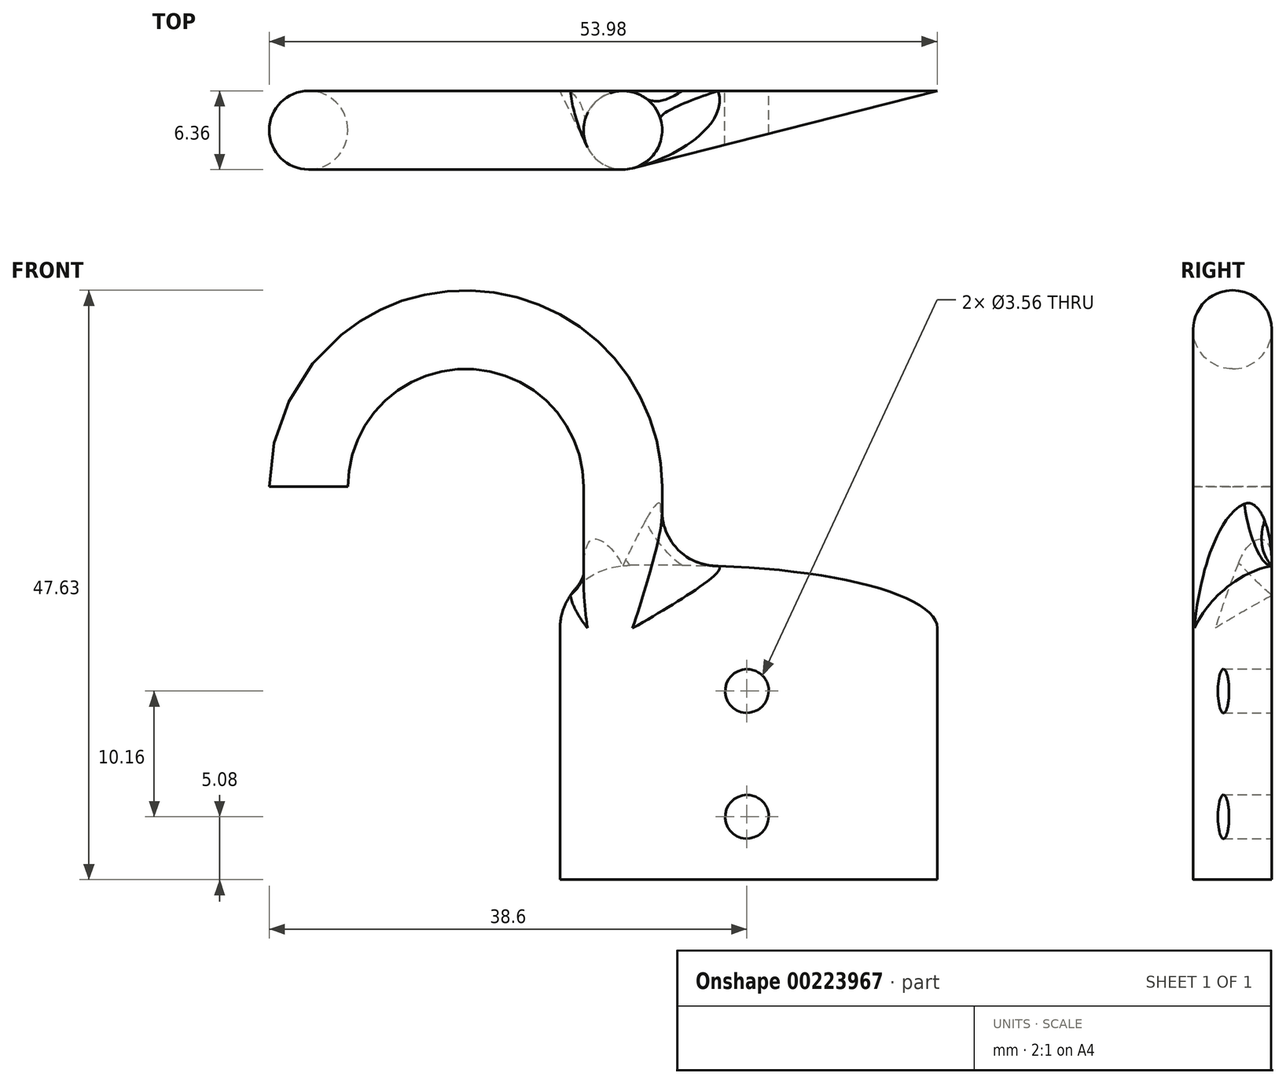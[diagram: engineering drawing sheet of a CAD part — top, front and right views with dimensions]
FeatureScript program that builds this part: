
annotation { "Feature Type Name" : "Feature", "Feature Type Description" : "" }
export const myFeature = defineFeature(function(context is Context, id is Id, definition is map)
    precondition{}
    {
        {
            var Q0;
            Q0=qCreatedBy(makeId("Top.planeOp"),FACE);
            var sketch = newSketch(context, id + "F0", { "sketchPlane" : qUnion([Q0])});
            skCircle(sketch, "E0", {"center": v(-12.7, 0) * mm, "radius": 3.17 * mm});
            skLineSegment(sketch, "E1", {"start": v(0, 67.95) * mm, "end": v(0, -27.2) * mm});
            skSolve(sketch);
        }
        {
            var Q0;
            Q0=makeQuery(id+"F0.imprint","IMPRINT",FACE,{"disambiguationData":[TD([[makeQuery(id+"F0.imprint","IMPRINT",EDGE,{"derivedFrom":sQuery(id+"F0.wireOp",EDGE,"E0")}),1.0]])]});
            var Q1;
            Q1=sQuery(id+"F0.wireOp",EDGE,"E1");
            revolve(context, id + "F1", {"entities" : qUnion([Q0]), "axis" : qUnion([Q1]), "revolveType" : RevolveType.ONE_DIRECTION, "oppositeDirection" : true, "angle" : 180 * degree});
        }
        {
            var Q0;
            Q0=makeQuery(id+"F1.opRevolve","CAP_FACE",FACE,{"disambiguationData":[OSD([sQuery(id+"F0.wireOp",EDGE,"E0")])],"isStart":false});
            extrude(context, id + "F2", {"entities" : qUnion([Q0]), "operationType" : NewBodyOperationType.ADD, "depth" : 6.35 * mm});
        }
        {
            var Q0;
            Q0=makeQuery(id+"F2.opExtrude","CAP_FACE",FACE,{"disambiguationData":[OSD([sQuery(id+"F0.wireOp",EDGE,"E0")])],"isStart":false});
            var sketch = newSketch(context, id + "F3", { "sketchPlane" : qUnion([Q0])});
            skCircle(sketch, "E2.0", {"center": v(12.7, 0) * mm, "radius": 3.17 * mm});
            skLineSegment(sketch, "E3", {"start": v(9.85, 1.4) * mm, "end": v(7.62, -3.17) * mm});
            skLineSegment(sketch, "E4", {"start": v(13.48, 3.08) * mm, "end": v(38.1, -3.17) * mm});
            skLineSegment(sketch, "E5", {"start": v(38.1, -3.17) * mm, "end": v(7.62, -3.17) * mm});
            skSolve(sketch);
        }
        {
            var Q0;
            {var subQ0=sQuery(id+"F3.wireOp",EDGE,"E4");Q0=makeQuery(id+"F3.imprint","IMPRINT",FACE,{"disambiguationData":[TD([[makeQuery(id+"F3.imprint","IMPRINT",EDGE,{"derivedFrom":subQ0}),-1.0]])]});}
            var Q1;
            {var subQ0=sQuery(id+"F3.wireOp",EDGE,"E2.0");var subQ1=makeQuery(id+"F3.imprint","INTERSECT",VERTEX,{"derivedFrom":[subQ0,sQuery(id+"F3.wireOp",EDGE,"E4")]});Q1=makeQuery(id+"F3.imprint","IMPRINT",FACE,{"disambiguationData":[TD([[makeQuery(id+"F3.imprint","IMPRINT",EDGE,{"disambiguationData":[TD([[subQ1,1.0]])],"derivedFrom":subQ0}),1.0]])]});}
            var Q2;
            {var subQ0=sQuery(id+"F3.wireOp",EDGE,"E3");Q2=makeQuery(id+"F3.imprint","IMPRINT",FACE,{"disambiguationData":[TD([[makeQuery(id+"F3.imprint","IMPRINT",EDGE,{"derivedFrom":subQ0}),1.0]])]});}
            extrude(context, id + "F7", {"entities" : qUnion([Q0, Q1, Q2]), "operationType" : NewBodyOperationType.ADD, "depth" : 25.4 * mm});
        }
        {
            var Q0;
            Q0=makeQuery(id+"F7.opExtrude","CAP_EDGE",EDGE,{"disambiguationData":[OSD([sQuery(id+"F3.wireOp",EDGE,"E4")])],"isStart":true});
            var Q1;
            Q1=makeQuery(id+"F7.opExtrude","CAP_EDGE",EDGE,{"disambiguationData":[OSD([sQuery(id+"F3.wireOp",EDGE,"E3")])],"isStart":true});
            fillet(context, id + "F4", {"entities" : qUnion([Q0, Q1]), "radius" : 5.08 * mm, "tangentPropagation" : true, "allowEdgeOverflow" : false});
        }
        {
            var Q0;
            Q0=makeQuery(id+"F4.opFillet","BLEND_EDGE",EDGE,{"blendedFrom":[makeQuery(id+"F7.opExtrude","CAP_EDGE",EDGE,{"disambiguationData":[OSD([sQuery(id+"F3.wireOp",EDGE,"E4")])],"isStart":true}),makeQuery(id+"F7.boolean.opBoolean","MERGE",FACE,{"derivedFrom":[makeQuery(id+"F2.opExtrude","SWEPT_FACE",FACE,{"disambiguationData":[OSD([sQuery(id+"F0.wireOp",EDGE,"E0")])]}),makeQuery(id+"F7.opExtrude","SWEPT_FACE",FACE,{"disambiguationData":[OSD([sQuery(id+"F3.wireOp",EDGE,"E2.0")])]})]})],"blendedInto":[makeQuery(id+"F7.boolean.opBoolean","MERGE",FACE,{"derivedFrom":[makeQuery(id+"F2.opExtrude","SWEPT_FACE",FACE,{"disambiguationData":[OSD([sQuery(id+"F0.wireOp",EDGE,"E0")])]}),makeQuery(id+"F7.opExtrude","SWEPT_FACE",FACE,{"disambiguationData":[OSD([sQuery(id+"F3.wireOp",EDGE,"E2.0")])]})]})]});
            fillet(context, id + "F8", {"entities" : qUnion([Q0]), "radius" : 5.08 * mm, "tangentPropagation" : true, "allowEdgeOverflow" : false});
        }
        {
            var Q0;
            Q0=makeQuery(id+"F7.opExtrude","SWEPT_FACE",FACE,{"disambiguationData":[OSD([sQuery(id+"F3.wireOp",EDGE,"E5")])]});
            var sketch = newSketch(context, id + "F5", { "sketchPlane" : qUnion([Q0])});
            skCircle(sketch, "E6", {"center": v(-22.72, -26.67) * mm, "radius": 1.78 * mm});
            skPoint(sketch, "E6.centerSnap0", {"position": v(-22.86, -31.75) * mm});
            skCircle(sketch, "E7", {"center": v(-22.72, -16.51) * mm, "radius": 1.78 * mm});
            skLineSegment(sketch, "E8", {"start": v(-38.1, -21.6) * mm, "end": v(-7.62, -21.6) * mm});
            skSolve(sketch);
        }
        {
            var Q0;
            Q0=makeQuery(id+"F5.imprint","IMPRINT",FACE,{"disambiguationData":[TD([[makeQuery(id+"F5.imprint","IMPRINT",EDGE,{"derivedFrom":sQuery(id+"F5.wireOp",EDGE,"E6")}),1.0]])]});
            var Q1;
            Q1=makeQuery(id+"F5.imprint","IMPRINT",FACE,{"disambiguationData":[TD([[makeQuery(id+"F5.imprint","IMPRINT",EDGE,{"derivedFrom":sQuery(id+"F5.wireOp",EDGE,"E7")}),1.0]])]});
            var Q2;
            Q2=makeQuery(id+"F7.opExtrude","SWEPT_FACE",FACE,{"disambiguationData":[OSD([sQuery(id+"F3.wireOp",EDGE,"E4")])]});
            extrude(context, id + "F6", {"entities" : qUnion([Q0, Q1]), "operationType" : NewBodyOperationType.REMOVE, "endBound" : BoundingType.UP_TO_SURFACE, "oppositeDirection" : true, "endBoundEntityFace" : qUnion([Q2]), "depth" : 25.4 * mm});
        }
    });
